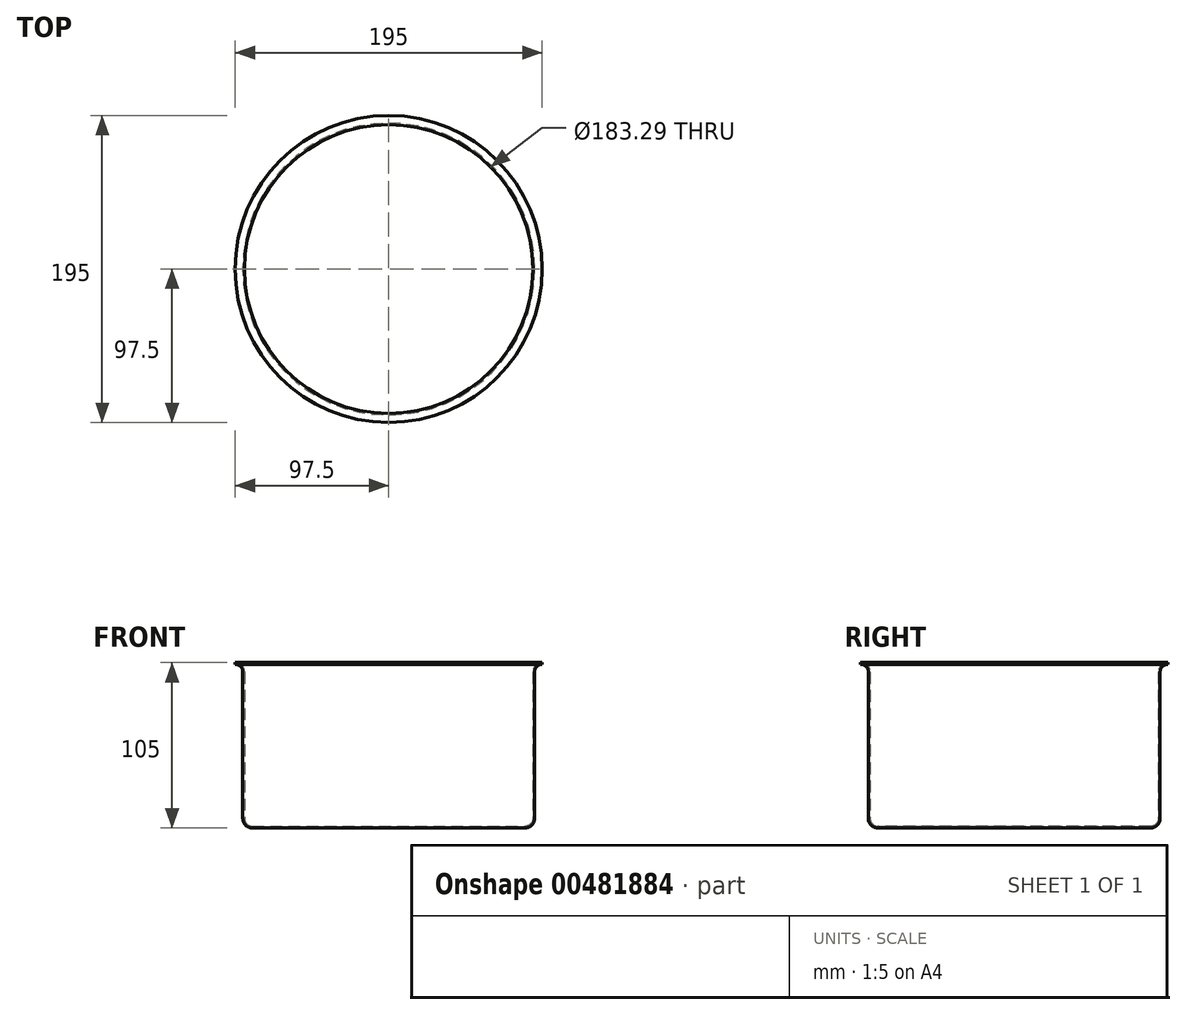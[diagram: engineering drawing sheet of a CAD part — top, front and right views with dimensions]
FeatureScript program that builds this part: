
annotation { "Feature Type Name" : "Feature", "Feature Type Description" : "" }
export const myFeature = defineFeature(function(context is Context, id is Id, definition is map)
    precondition{}
    {
        {
            var Q0;
            Q0=qCreatedBy(makeId("Front.planeOp"),FACE);
            var sketch = newSketch(context, id + "F0", { "sketchPlane" : qUnion([Q0])});
            skLineSegment(sketch, "E0", {"start": v(0, 0) * mm, "end": v(0, 1) * mm});
            skLineSegment(sketch, "E1", {"start": v(0, 0) * mm, "end": v(-86.64, 0) * mm});
            skArc(sketch, "E2", {"start": v(-86.64, 0) * mm, "mid": v(-90.89, 1.76) * mm, "end": v(-92.64, 6) * mm});
            skLineSegment(sketch, "E3", {"start": v(-92.64, 6) * mm, "end": v(-92.64, 99.07) * mm});
            skArc(sketch, "E4", {"start": v(-92.64, 99.07) * mm, "mid": v(-94.06, 102.53) * mm, "end": v(-97.5, 104) * mm});
            skLineSegment(sketch, "E5", {"start": v(-97.5, 104) * mm, "end": v(-97.5, 105) * mm});
            skArc(sketch, "E6.1", {"start": v(-91.64, 99.07) * mm, "mid": v(-93.35, 103.24) * mm, "end": v(-97.5, 105) * mm});
            skLineSegment(sketch, "E6.2", {"start": v(-91.64, 6) * mm, "end": v(-91.64, 99.07) * mm});
            skLineSegment(sketch, "E6.3", {"start": v(0, 1) * mm, "end": v(-86.64, 1) * mm});
            skPoint(sketch, "E7.visualSharp", {"position": v(-91.64, 1) * mm});
            skArc(sketch, "E7.filletArc", {"start": v(-91.64, 6) * mm, "mid": v(-90.18, 2.46) * mm, "end": v(-86.64, 1) * mm});
            skSolve(sketch);
        }
        {
            var Q0;
            Q0 = qSketchRegion(id + "F0", true);
            var Q1;
            Q1=sQuery(id+"F0.wireOp",EDGE,"E0");
            revolve(context, id + "F1", {"entities" : qUnion([Q0]), "axis" : qUnion([Q1]), "revolveType" : RevolveType.FULL});
        }
    });
